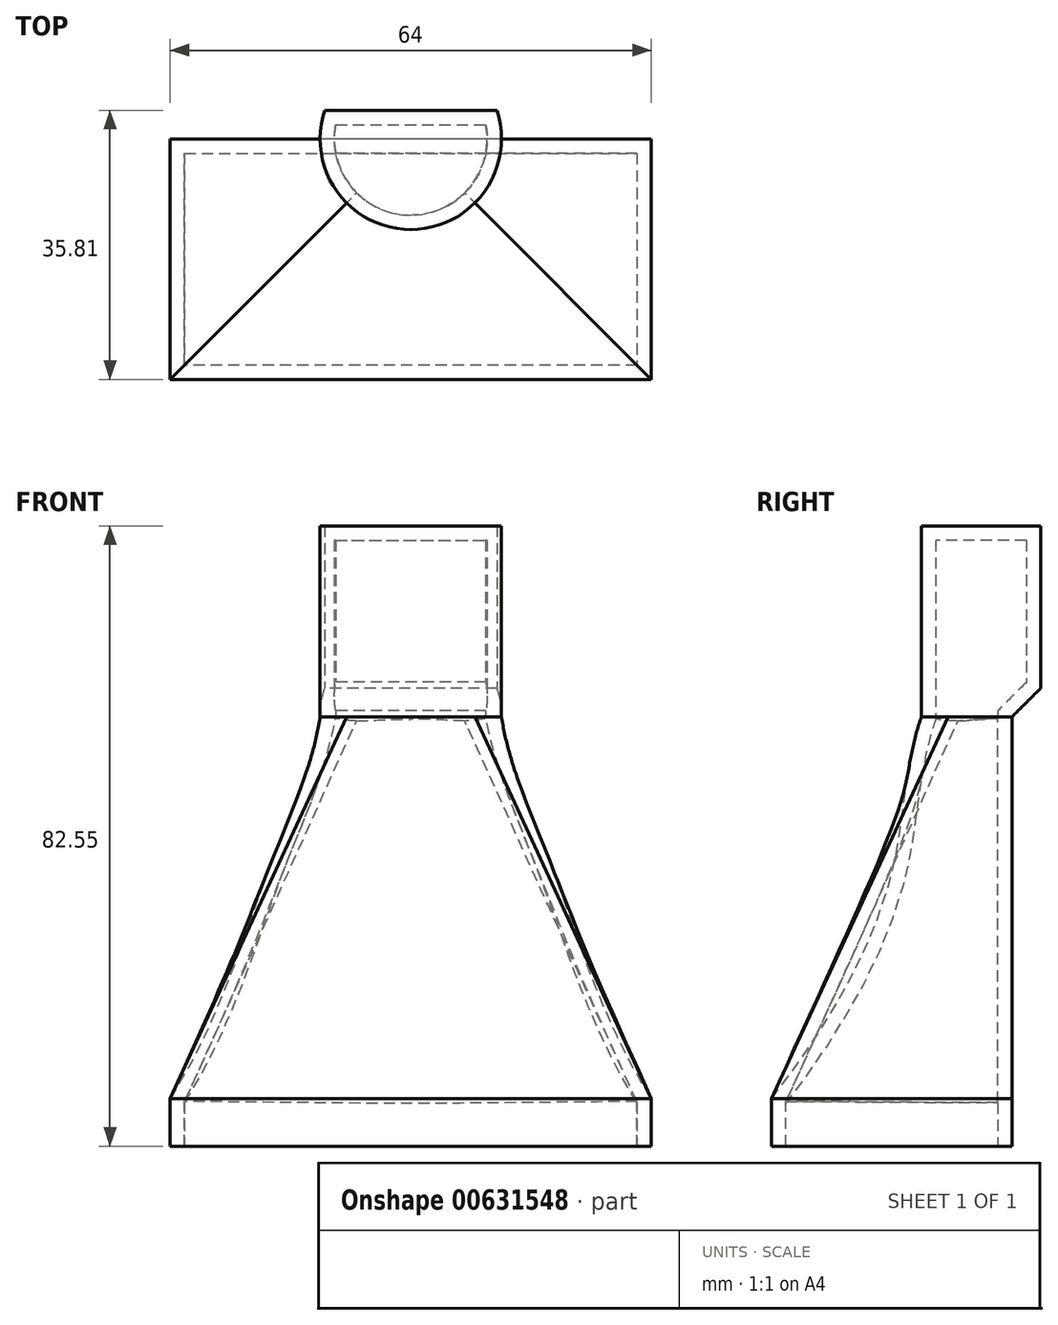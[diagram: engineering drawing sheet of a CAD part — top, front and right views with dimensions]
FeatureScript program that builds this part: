
annotation { "Feature Type Name" : "Feature", "Feature Type Description" : "" }
export const myFeature = defineFeature(function(context is Context, id is Id, definition is map)
    precondition{}
    {
        {
            var Q0;
            Q0=qCreatedBy(makeId("Top.planeOp"),FACE);
            var sketch = newSketch(context, id + "F0", { "sketchPlane" : qUnion([Q0])});
            skLineSegment(sketch, "E0.bottom", {"start": v(32, 16) * mm, "end": v(-32, 16) * mm});
            skLineSegment(sketch, "E0.top", {"start": v(32, -16) * mm, "end": v(-32, -16) * mm});
            skLineSegment(sketch, "E0.left", {"start": v(32, 16) * mm, "end": v(32, -16) * mm});
            skLineSegment(sketch, "E0.right", {"start": v(-32, 16) * mm, "end": v(-32, -16) * mm});
            skPoint(sketch, "E0.middle", {"position": v(0, 0) * mm});
            skSolve(sketch);
        }
        {
            var Q0;
            Q0=qCreatedBy(makeId("Top.planeOp"),FACE);
            cPlane(context, id + "F1", {"entities" : qUnion([Q0]), "cplaneType" : CPlaneType.OFFSET, "offset" : 50.8 * mm, "width" : 152.4 * mm, "height" : 152.4 * mm});
        }
        {
            var Q0;
            Q0=qCreatedBy(id+"F1.planeOp",FACE);
            var sketch = newSketch(context, id + "F2", { "sketchPlane" : qUnion([Q0])});
            skPoint(sketch, "E1.0", {"position": v(0, 16) * mm});
            skLineSegment(sketch, "E2.0", {"start": v(32, 16) * mm, "end": v(-32, 16) * mm});
            skArc(sketch, "E3", {"start": v(-12.06, 16) * mm, "mid": v(0, 3.94) * mm, "end": v(12.07, 16) * mm});
            skLineSegment(sketch, "E4", {"start": v(-12.06, 16) * mm, "end": v(12.07, 16) * mm});
            skArc(sketch, "E5", {"start": v(12.07, 16) * mm, "mid": v(11.9, 17.93) * mm, "end": v(11.45, 19.81) * mm});
            skLineSegment(sketch, "E6", {"start": v(-11.45, 19.81) * mm, "end": v(11.45, 19.81) * mm});
            skArc(sketch, "E7.trimOffspring", {"start": v(-11.45, 19.81) * mm, "mid": v(-11.9, 17.93) * mm, "end": v(-12.06, 16) * mm});
            skSolve(sketch);
        }
        {
            var Q0;
            Q0=qCreatedBy(id+"F1.planeOp",FACE);
            cPlane(context, id + "F3", {"entities" : qUnion([Q0]), "cplaneType" : CPlaneType.OFFSET, "offset" : 25.4 * mm, "width" : 152.4 * mm, "height" : 152.4 * mm});
        }
        {
            var Q0;
            Q0=qCreatedBy(id+"F3.planeOp",FACE);
            var sketch = newSketch(context, id + "F4", { "sketchPlane" : qUnion([Q0])});
            skArc(sketch, "E8.0.0", {"start": v(-11.45, 19.81) * mm, "mid": v(-11.9, 17.93) * mm, "end": v(-12.06, 16) * mm});
            skLineSegment(sketch, "E8.0.1", {"start": v(-12.06, 16) * mm, "end": v(12.07, 16) * mm});
            skArc(sketch, "E8.0.2", {"start": v(12.07, 16) * mm, "mid": v(11.9, 17.93) * mm, "end": v(11.45, 19.81) * mm});
            skLineSegment(sketch, "E8.0.3", {"start": v(11.45, 19.81) * mm, "end": v(-11.45, 19.81) * mm});
            skLineSegment(sketch, "E9.0.0", {"start": v(12.07, 16) * mm, "end": v(-12.06, 16) * mm});
            skArc(sketch, "E9.0.1", {"start": v(-12.06, 16) * mm, "mid": v(0, 3.94) * mm, "end": v(12.07, 16) * mm});
            skSolve(sketch);
        }
        {
            var Q0;
            Q0=qCreatedBy(id+"F3.planeOp",FACE);
            cPlane(context, id + "F5", {"entities" : qUnion([Q0]), "cplaneType" : CPlaneType.OFFSET, "offset" : 6.35 * mm, "width" : 152.4 * mm, "height" : 152.4 * mm});
        }
        {
            var Q0;
            Q0=makeQuery(id+"F2.imprint","IMPRINT",FACE,{"disambiguationData":[TD([[makeQuery(id+"F2.imprint","IMPRINT",EDGE,{"derivedFrom":sQuery(id+"F2.wireOp",EDGE,"E5")}),1.0]])]});
            var Q1;
            Q1=makeQuery(id+"F2.imprint","IMPRINT",FACE,{"disambiguationData":[TD([[makeQuery(id+"F2.imprint","IMPRINT",EDGE,{"derivedFrom":sQuery(id+"F2.wireOp",EDGE,"E3")}),1.0]])]});
            var Q2;
            Q2=qCreatedBy(id+"F3.planeOp",FACE);
            extrude(context, id + "F6", {"entities" : qUnion([Q0, Q1]), "endBound" : BoundingType.UP_TO_SURFACE, "depth" : 25.4 * mm, "endBoundEntityFace" : qUnion([Q2]), "offsetDistance" : 25.4 * mm});
        }
        {
            var Q0;
            Q0=qCreatedBy(makeId("Right.planeOp"),FACE);
            var sketch = newSketch(context, id + "F7", { "sketchPlane" : qUnion([Q0])});
            skPoint(sketch, "E10.0", {"position": v(16, 50.8) * mm});
            skPoint(sketch, "E11.0", {"position": v(3.94, 50.8) * mm});
            skPoint(sketch, "E12.0", {"position": v(16, 0) * mm});
            skPoint(sketch, "E13.0", {"position": v(-16, 0) * mm});
            skLineSegment(sketch, "E14", {"start": v(16, 0) * mm, "end": v(16, 50.8) * mm});
            skFitSpline(sketch, "E15", {"points": [v(-16, 0) * mm, v(0, 30) * mm, v(3.94, 50.8) * mm], "startDerivative": vector(43.46, 55.16) * mm, "endDerivative": vector(16.05, 46.07) * mm});
            skSolve(sketch);
        }
        {
            var Q0;
            Q0=sQuery(id+"F2.wireOp",EDGE,"E4");
            cPoint(context, id + "F8", {"entities" : qUnion([Q0]), "parameter" : 0.5});
        }
        {
            var Q0;
            Q0=sQuery(id+"F0.wireOp",VERTEX,"E0.right.start");
            var Q1;
            Q1=sQuery(id+"F0.wireOp",VERTEX,"E0.left.start");
            var Q2;
            Q2 = qCreatedBy(id + "F8" ,VERTEX);
            cPlane(context, id + "F9", {"entities" : qUnion([Q0, Q1, Q2]), "cplaneType" : CPlaneType.THREE_POINT, "offset" : 25.4 * mm, "width" : 152.4 * mm, "height" : 152.4 * mm});
        }
        {
            var Q0;
            Q0=qCreatedBy(id+"F9.planeOp",FACE);
            var sketch = newSketch(context, id + "F10", { "sketchPlane" : qUnion([Q0])});
            skPoint(sketch, "E16.0", {"position": v(-32, 0) * mm});
            skPoint(sketch, "E17.0", {"position": v(32, 0) * mm});
            skPoint(sketch, "E18.0", {"position": v(0, 50.8) * mm});
            skPoint(sketch, "E19.0", {"position": v(0, 30) * mm});
            skPoint(sketch, "E20.0", {"position": v(-12.07, 50.8) * mm});
            skPoint(sketch, "E21.0", {"position": v(12.06, 50.8) * mm});
            skFitSpline(sketch, "E22", {"points": [v(-32, 0) * mm, v(-19.05, 30) * mm, v(-12.07, 50.8) * mm], "startDerivative": vector(35.3, 55.46) * mm, "endDerivative": vector(7.07, 45.76) * mm});
            skFitSpline(sketch, "E23", {"points": [v(32, 0) * mm, v(19.05, 30) * mm, v(12.06, 50.8) * mm], "startDerivative": vector(-35.63, 55.4) * mm, "endDerivative": vector(-6.7, 45.82) * mm});
            skSolve(sketch);
        }
        {
            var Q1;
            Q1=makeQuery(id+"F0.imprint","IMPRINT",FACE,{"disambiguationData":[TD([[makeQuery(id+"F0.imprint","IMPRINT",EDGE,{"derivedFrom":sQuery(id+"F0.wireOp",EDGE,"E0.bottom")}),1.0]])]});
            var Q2;
            Q2=makeQuery(id+"F2.imprint","IMPRINT",FACE,{"disambiguationData":[TD([[makeQuery(id+"F2.imprint","IMPRINT",EDGE,{"derivedFrom":sQuery(id+"F2.wireOp",EDGE,"E3")}),1.0]])]});
            var Q3;
            Q3=sQuery(id+"F7.wireOp",EDGE,"E14");
            var Q4;
            Q4=sQuery(id+"F7.wireOp",EDGE,"E15");
            var Q5;
            Q5=sQuery(id+"F10.wireOp",EDGE,"E23");
            var Q6;
            Q6=sQuery(id+"F10.wireOp",EDGE,"E22");
            loft(context, id + "F11", {"operationType" : NewBodyOperationType.ADD, "addGuides" : true, "sheetProfilesArray" : [{ "sheetProfileEntities" : qUnion([Q1]) }, { "sheetProfileEntities" : qUnion([Q2]) }], "guidesArray" : [{ "guideEntities" : qUnion([Q3]), "guideDerivativeType" : LoftGuideDerivativeType.DEFAULT, "guideDerivativeMagnitude" : 1 }, { "guideEntities" : qUnion([Q4]), "guideDerivativeType" : LoftGuideDerivativeType.DEFAULT, "guideDerivativeMagnitude" : 1 }, { "guideEntities" : qUnion([Q5]), "guideDerivativeType" : LoftGuideDerivativeType.DEFAULT, "guideDerivativeMagnitude" : 1 }, { "guideEntities" : qUnion([Q6]), "guideDerivativeType" : LoftGuideDerivativeType.DEFAULT, "guideDerivativeMagnitude" : 1 }]});
        }
        {
            var Q0;
            Q0=makeQuery(id+"F0.imprint","IMPRINT",FACE,{"disambiguationData":[TD([[makeQuery(id+"F0.imprint","IMPRINT",EDGE,{"derivedFrom":sQuery(id+"F0.wireOp",EDGE,"E0.bottom")}),1.0]])]});
            extrude(context, id + "F12", {"entities" : qUnion([Q0]), "operationType" : NewBodyOperationType.ADD, "oppositeDirection" : true, "depth" : 6.35 * mm, "offsetDistance" : 25.4 * mm});
        }
        {
            var Q0;
            Q0=makeQuery(id+"F6.opExtrude","CAP_EDGE",EDGE,{"disambiguationData":[OSD([sQuery(id+"F2.wireOp",EDGE,"E6")])],"isStart":true});
            chamfer(context, id + "F13", {"entities" : qUnion([Q0]), "width" : 3.8 * mm, "tangentPropagation" : true});
        }
        {
            var Q0;
            Q0=makeQuery(id+"F12.opExtrude","CAP_FACE",FACE,{"disambiguationData":[OSD([sQuery(id+"F0.wireOp",EDGE,"E0.bottom"),sQuery(id+"F0.wireOp",EDGE,"E0.top"),sQuery(id+"F0.wireOp",EDGE,"E0.left"),sQuery(id+"F0.wireOp",EDGE,"E0.right")])],"isStart":false});
            var Q1;
            Q1=makeQuery(id+"F6.opExtrude","CAP_FACE",FACE,{"disambiguationData":[OSD([dummyQuery(id+"F3.planeOp",FACE)])],"isStart":false});
            shell(context, id + "F14", {"entities" : qUnion([Q0, Q1]), "thickness" : 1.9 * mm});
        }
    });
